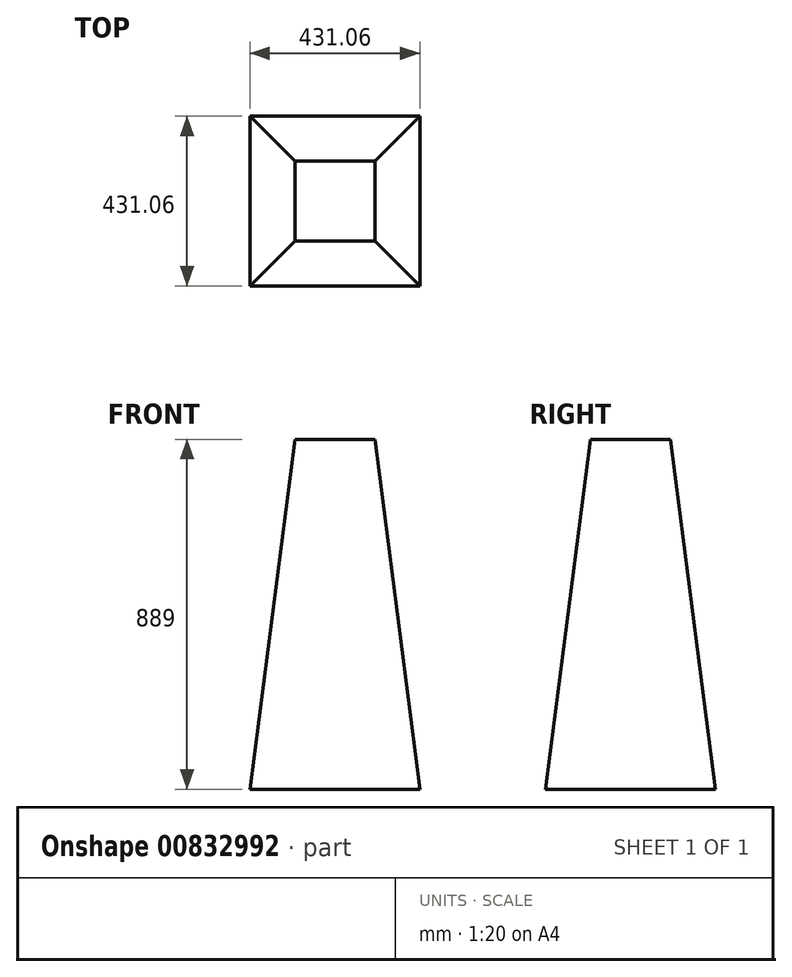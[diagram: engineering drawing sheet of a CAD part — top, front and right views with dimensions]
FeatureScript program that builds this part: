
annotation { "Feature Type Name" : "Feature", "Feature Type Description" : "" }
export const myFeature = defineFeature(function(context is Context, id is Id, definition is map)
    precondition{}
    {
        {
            var Q0;
            Q0=qCreatedBy(makeId("Top.planeOp"),FACE);
            var sketch = newSketch(context, id + "F0", { "sketchPlane" : qUnion([Q0])});
            skCircle(sketch, "E0", {"center": v(0, 0) * mm, "radius": 304.8 * mm, "construction": true});
            skLineSegment(sketch, "E1.bottom", {"start": v(215.53, 215.53) * mm, "end": v(-215.53, 215.53) * mm});
            skLineSegment(sketch, "E1.top", {"start": v(215.53, -215.53) * mm, "end": v(-215.53, -215.53) * mm});
            skLineSegment(sketch, "E1.left", {"start": v(215.53, 215.53) * mm, "end": v(215.53, -215.53) * mm});
            skLineSegment(sketch, "E1.right", {"start": v(-215.53, 215.53) * mm, "end": v(-215.53, -215.53) * mm});
            skSolve(sketch);
        }
        {
            var Q0;
            Q0=qCreatedBy(makeId("Top.planeOp"),FACE);
            cPlane(context, id + "F1", {"entities" : qUnion([Q0]), "cplaneType" : CPlaneType.OFFSET, "offset" : 889 * mm, "width" : 152.4 * mm, "height" : 152.4 * mm});
        }
        {
            var Q0;
            Q0=qCreatedBy(id+"F1.planeOp",FACE);
            var sketch = newSketch(context, id + "F2", { "sketchPlane" : qUnion([Q0])});
            skCircle(sketch, "E2", {"center": v(0, 0) * mm, "radius": 457.2 * mm, "construction": true});
            skLineSegment(sketch, "E3.bottom", {"start": v(101.6, 101.6) * mm, "end": v(-101.6, 101.6) * mm});
            skLineSegment(sketch, "E3.top", {"start": v(101.6, -101.6) * mm, "end": v(-101.6, -101.6) * mm});
            skLineSegment(sketch, "E3.left", {"start": v(101.6, 101.6) * mm, "end": v(101.6, -101.6) * mm});
            skLineSegment(sketch, "E3.right", {"start": v(-101.6, 101.6) * mm, "end": v(-101.6, -101.6) * mm});
            skSolve(sketch);
        }
        {
            var Q0;
            Q0=makeQuery(id+"F2.imprint","IMPRINT",FACE,{"disambiguationData":[TD([[makeQuery(id+"F2.imprint","IMPRINT",EDGE,{"derivedFrom":sQuery(id+"F2.wireOp",EDGE,"E3.bottom")}),1.0]])]});
            var Q1;
            Q1=makeQuery(id+"F0.imprint","IMPRINT",FACE,{"disambiguationData":[TD([[makeQuery(id+"F0.imprint","IMPRINT",EDGE,{"derivedFrom":sQuery(id+"F0.wireOp",EDGE,"E1.bottom")}),1.0]])]});
            loft(context, id + "F3", {"sheetProfilesArray" : [{ "sheetProfileEntities" : qUnion([Q0]) }, { "sheetProfileEntities" : qUnion([Q1]) }]});
        }
    });
